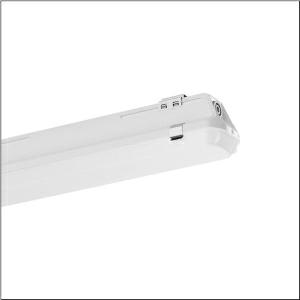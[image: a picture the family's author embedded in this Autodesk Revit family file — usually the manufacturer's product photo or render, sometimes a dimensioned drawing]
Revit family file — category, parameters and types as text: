
# Revit family: monsun_r__11_51fp10ep430h_21f7
name_source: partatom
category: Lighting Fixtures
units: mm (PartAtom-declared; Revit-internal decimal feet)

## family parameters
Cut with Voids When Loaded = No
Host = Face
Light Source = No
Part Type = Normal
Room Calculation Point = No
Round Connector Dimension = Use Diameter
Shared = No

## types (1)
- --- (1 x LED, 3840 lm, 22.3 W, 4000K)
    Apparent Load = 22 VA
    CIE Flux Codes = 47 77 93 94 100
    Color Rendering = 80
    Color Temperature = 4000K
    Default Elevation = 1800 mm
    Description = Monsun® 11, damp-proof luminaire, chain hanger, primary optical cover: enclosure, of PMMA, light emission: direct distribution, primary light characteristic: symmetric, installation type: suspended mounting, surface-mounted, horizontal mounting, vertical mounting, LED, rated luminous flux: 3.840lm, luminous efficacy: 172lm/W, light colour: 840, colour temperature: 4000K, control gear: ECG DALI, with terminal, 5-pole, max. 2.5mm², mains connection: 220..240V, AC, 50/60Hz, rated input power: 22W, luminaire housing, of glass-fibre reinforced polyester, uncoated, bright grey, incl. chain hanger, length: 1.590mm, width: 90mm, height: 88mm, clip for enclosure, of stainless steel (V2A), ceiling mounting element, of stainless steel (V2A), chain hanger, of stainless steel (V2A), protection rating (complete): IP66, insulation class (complete): insulation class I (protective earthing), certification: CE, ENEC, VDE, UKCA, protection symbol: D, impact resistance: IK04, permissible operating ambient temperature: -25..+40°C, standard: EN 50419, EN 60598-2-1, no direct snow, no direct sun, no direct rain, for indoor or canopied outdoor use, corresponds to IFS (International Featured Standards) requirements for safety and quality in the food industry, contact your sales advisor before using the luminaires in applications with unclear chemical exposure, large temperature fluctuations or condensation-forming humidity, LABS conformity tested according to VDMA 24364:2018-05, packaging unit: 1 piece
    Height = 89 mm
    Lamp = 1 x LED
    Lamp Light Flux = 3840 lm
    Lamp Power = 22.3 W
    Lamp count = 1
    Length = 1590 mm
    Luminous efficacy = 172 lm/W
    Manufacturer = Siteco
    ModVariant = No
    Model = 51FP10EP430H
    Mounting Place = Ceiling
    Mounting Type = Surface mounted
    Number of Poles = 1
    OnlyDefault = Yes
    Power Factor = 1
    Product Name = Monsun® 11
    Product group = damp-proof luminaire
    ProductGroupID = 300
    Protection Class = Protection class I
    Protection Degree = IP 66
    RLX_Detail_Level = 1
    RLX_Emergency_Light_Flux = 0 lm
    RLX_Emergency_Type = 0
    RLX_Emergency_Type_DB = No
    RlxData = <blob elided: 92053 chars, md5=9710f748>
    Socket = socket
    Standby Power = 0 W
    System Light Flux = 3840 lm
    System Power = 22 W
    Type Comments = factory setting: luminous flux: 100 % | dim-lin: 254 | 145 mA
    Type Image = l_1004748.jpg
    URL = http://relux.com
    VarID = @adj_142309
    Voltage = 0 V
    Weight = 0.00 kg
    Width = 90 mm

## geometry (parser evidence)
native form markers: Blend x4, Sweep x15
no freeform markers — native parametric forms only
